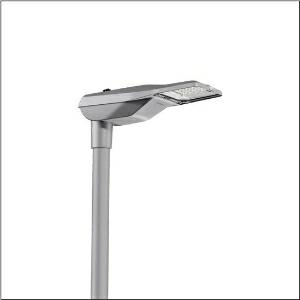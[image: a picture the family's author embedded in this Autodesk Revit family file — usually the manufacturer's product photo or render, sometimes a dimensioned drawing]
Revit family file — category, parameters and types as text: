
# Revit family: streetlight_sl_21_iq_micro___p0_8ab_5xe1r31v08db_6cb1
name_source: partatom
category: Lighting Fixtures
units: mm (PartAtom-declared; Revit-internal decimal feet)

## family parameters
Cut with Voids When Loaded = No
Host = Face
Light Source = No
Part Type = Normal
Room Calculation Point = No
Round Connector Dimension = Use Diameter
Shared = No

## types (1)
- --- (1 x LED, 4550 lm, 39.1 W, 3000K)
    Apparent Load = 39 VA
    CIE Flux Codes = 36 71 98 100 100
    Color Rendering = 70
    Color Temperature = 3000K
    Default Elevation = 1800 mm
    Description = Streetlight SL 21 iQ micro, mast luminaire, primary light control with lens, of PMMA, primary optical cover: cover, of toughened safety glass, transparent, light distribution: P0.8aB, light emission: direct distribution, primary light characteristic: asymmetric, installation type: post-top, side-entry, LED, High Power LED, rated luminous flux: 4.550lm, luminous efficacy: 116lm/W, light colour: 730, colour temperature: 3000K, control gear: iQ-Street Remote, D4i with power reduction, control: pre-setting: logarithmic dimming characteristic, Street-Remote, Auto-Match, Temp-Guard, Lumen-Switch, Night-Set, Smart-Wire, Light-Fading, Desk-Remote (wireless, voltage-free reading and setting of iQ features in the workshop via application-optimized NFC function/RFID function), optimised constant luminous flux control (CLO 2.0), mains connection: 220..240V, AC, 50/60Hz, start of lifetime: 39W, end of service life: 41W, reduction: 17W, luminaire housing, of diecast aluminium, powder-coated, Siteco® metallic grey (DB 702S), corrosivity category C5 mid according to DIN EN ISO 12944, please order mast flange separately, inclination adjustable: 0°, 5°, 10°, 15°, sealing non-destructively replaceable, multi-level sealing system, length: 528mm, width: 235mm, height: 110mm, mast flange for spigot size: 42mm (side-entry): 5XC10008XM4, 60/48mm (side-entry/post-top): 5XC10108XM2, 76/60mm (side-entry/post-top): 5XC10108XM1, mounting height: 4..8m, Smart Interface above, protection rating (complete): IP66, insulation class (complete): insulation class II (safety insulation), certification: CE, ENEC, ENEC+, VDE, impact resistance: IK09, permissible operating ambient temperature for outdoor applications: -40..+50°C, standard-compliant lighting for roads and squares, packaging unit: 1 piece

Light Distribution: P0.8aB
    Height = 110 mm
    Lamp = 1 x LED
    Lamp Light Flux = 4550 lm
    Lamp Power = 39.1 W
    Lamp count = 1
    Length = 528 mm
    Luminous efficacy = 116 lm/W
    Manufacturer = Siteco
    ModVariant = No
    Model = 5XE1R31V08DB
    Number of Poles = 1
    OnlyDefault = Yes
    Power Factor = 1
    Product Name = Streetlight SL 21 iQ micro | P0.8aB
    Product group = mast luminaire | pylon top
    ProductGroupID = 6100
    Protection Class = Protection class II
    Protection Degree = IP 66
    RLX_Detail_Level = 1
    RLX_Emergency_Light_Flux = 0 lm
    RLX_Emergency_Type = 0
    RLX_Emergency_Type_DB = No
    RlxData = <blob elided: 98549 chars, md5=eb6aff1a>
    Socket = socket
    Standby Power = 0 W
    System Light Flux = 4550 lm
    System Power = 39 W
    Type Comments = factory setting: luminous flux: 100 % | dim-lin: 254 | 765 mA
    Type Image = l_1277292.jpg
    URL = http://relux.com
    VarID = @adj_072808
    Voltage = 0 V
    Weight = 0.00 kg
    Width = 235 mm

## geometry (parser evidence)
native form markers: Blend x4, Sweep x11
no freeform markers — native parametric forms only
